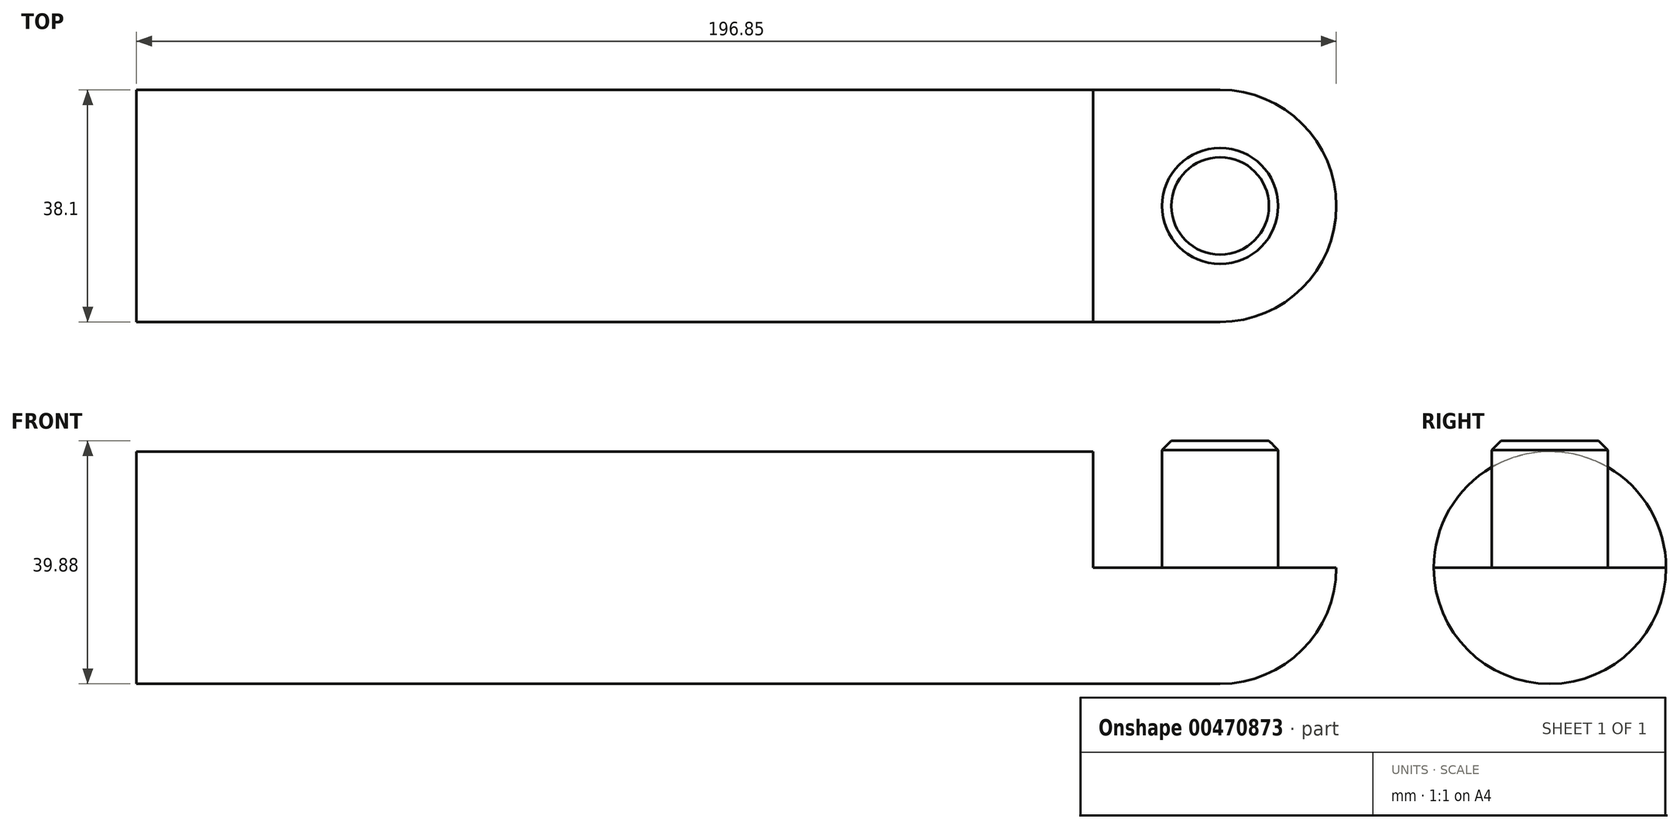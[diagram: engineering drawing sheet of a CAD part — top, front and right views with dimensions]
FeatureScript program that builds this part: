
annotation { "Feature Type Name" : "Feature", "Feature Type Description" : "" }
export const myFeature = defineFeature(function(context is Context, id is Id, definition is map)
    precondition{}
    {
        {
            var Q0;
            Q0=qCreatedBy(makeId("Front.planeOp"),FACE);
            var sketch = newSketch(context, id + "F0", { "sketchPlane" : qUnion([Q0])});
            skLineSegment(sketch, "E0", {"start": v(0, 0) * mm, "end": v(-177.8, 0) * mm});
            skLineSegment(sketch, "E1", {"start": v(-177.8, 0) * mm, "end": v(-177.8, 19.05) * mm});
            skLineSegment(sketch, "E2", {"start": v(-177.8, 19.05) * mm, "end": v(0, 19.05) * mm});
            skLineSegment(sketch, "E3", {"start": v(0, 19.05) * mm, "end": v(0, 0) * mm});
            skSolve(sketch);
        }
        {
            var Q0;
            Q0=makeQuery(id+"F0.imprint","IMPRINT",FACE,{"disambiguationData":[TD([[makeQuery(id+"F0.imprint","IMPRINT",EDGE,{"derivedFrom":sQuery(id+"F0.wireOp",EDGE,"E0")}),-1.0]])]});
            var Q1;
            Q1=sQuery(id+"F0.wireOp",EDGE,"E0");
            revolve(context, id + "F1", {"entities" : qUnion([Q0]), "axis" : qUnion([Q1]), "revolveType" : RevolveType.FULL});
        }
        {
            var Q0;
            Q0=qCreatedBy(makeId("Front.planeOp"),FACE);
            var sketch = newSketch(context, id + "F2", { "sketchPlane" : qUnion([Q0])});
            skLineSegment(sketch, "E4", {"start": v(0, 0) * mm, "end": v(-20.83, 0) * mm});
            skLineSegment(sketch, "E5", {"start": v(-20.83, 0) * mm, "end": v(-20.83, 20.83) * mm});
            skLineSegment(sketch, "E6", {"start": v(-20.83, 20.83) * mm, "end": v(0, 20.83) * mm});
            skLineSegment(sketch, "E7", {"start": v(0, 0) * mm, "end": v(0, 20.83) * mm});
            skSolve(sketch);
        }
        {
            var Q0;
            Q0=makeQuery(id+"F2.imprint","IMPRINT",FACE,{"disambiguationData":[TD([[makeQuery(id+"F2.imprint","IMPRINT",EDGE,{"derivedFrom":sQuery(id+"F2.wireOp",EDGE,"E4")}),-1.0]])]});
            extrude(context, id + "F3", {"entities" : qUnion([Q0]), "operationType" : NewBodyOperationType.REMOVE, "endBound" : BoundingType.SYMMETRIC, "oppositeDirection" : true, "depth" : 41.66 * mm});
        }
        {
            var Q0;
            Q0=qCreatedBy(makeId("Front.planeOp"),FACE);
            var sketch = newSketch(context, id + "F4", { "sketchPlane" : qUnion([Q0])});
            skLineSegment(sketch, "E8", {"start": v(0, 0) * mm, "end": v(19.05, 0) * mm});
            skArc(sketch, "E9", {"start": v(0, -19.05) * mm, "mid": v(13.47, -13.47) * mm, "end": v(19.05, 0) * mm});
            skLineSegment(sketch, "E10", {"start": v(0, 0) * mm, "end": v(0, -19.05) * mm});
            skSolve(sketch);
        }
        {
            var Q0;
            Q0=makeQuery(id+"F4.imprint","IMPRINT",FACE,{"disambiguationData":[TD([[makeQuery(id+"F4.imprint","IMPRINT",EDGE,{"derivedFrom":sQuery(id+"F4.wireOp",EDGE,"E8")}),-1.0]])]});
            var Q1;
            Q1=sQuery(id+"F4.wireOp",EDGE,"E10");
            revolve(context, id + "F5", {"operationType" : NewBodyOperationType.ADD, "entities" : qUnion([Q0]), "axis" : qUnion([Q1]), "revolveType" : RevolveType.FULL});
        }
        {
            var Q0;
            Q0=makeQuery(id+"F5.boolean.opBoolean","MERGE",FACE,{"derivedFrom":[makeQuery(id+"F3.boolean.opBoolean","COPY",FACE,{"derivedFrom":makeQuery(id+"F3.opExtrude","SWEPT_FACE",FACE,{"disambiguationData":[OSD([sQuery(id+"F2.wireOp",EDGE,"E4")])]})}),makeQuery(id+"F5.opRevolve","SWEPT_FACE",FACE,{"disambiguationData":[OSD([sQuery(id+"F4.wireOp",EDGE,"E8")])]})]});
            var sketch = newSketch(context, id + "F6", { "sketchPlane" : qUnion([Q0])});
            skCircle(sketch, "E11", {"center": v(0, 0) * mm, "radius": 9.53 * mm});
            skSolve(sketch);
        }
        {
            var Q0;
            Q0=makeQuery(id+"F6.imprint","IMPRINT",FACE,{"disambiguationData":[TD([[makeQuery(id+"F6.imprint","IMPRINT",EDGE,{"derivedFrom":sQuery(id+"F6.wireOp",EDGE,"E11")}),1.0]])]});
            extrude(context, id + "F7", {"entities" : qUnion([Q0]), "operationType" : NewBodyOperationType.ADD, "depth" : 20.83 * mm});
        }
        {
            var Q0;
            Q0=makeQuery(id+"F7.opExtrude","CAP_FACE",FACE,{"disambiguationData":[OSD([sQuery(id+"F6.wireOp",EDGE,"E11")])],"isStart":false});
            chamfer(context, id + "F8", {"entities" : qUnion([Q0]), "width" : 1.52 * mm, "tangentPropagation" : true});
        }
    });
